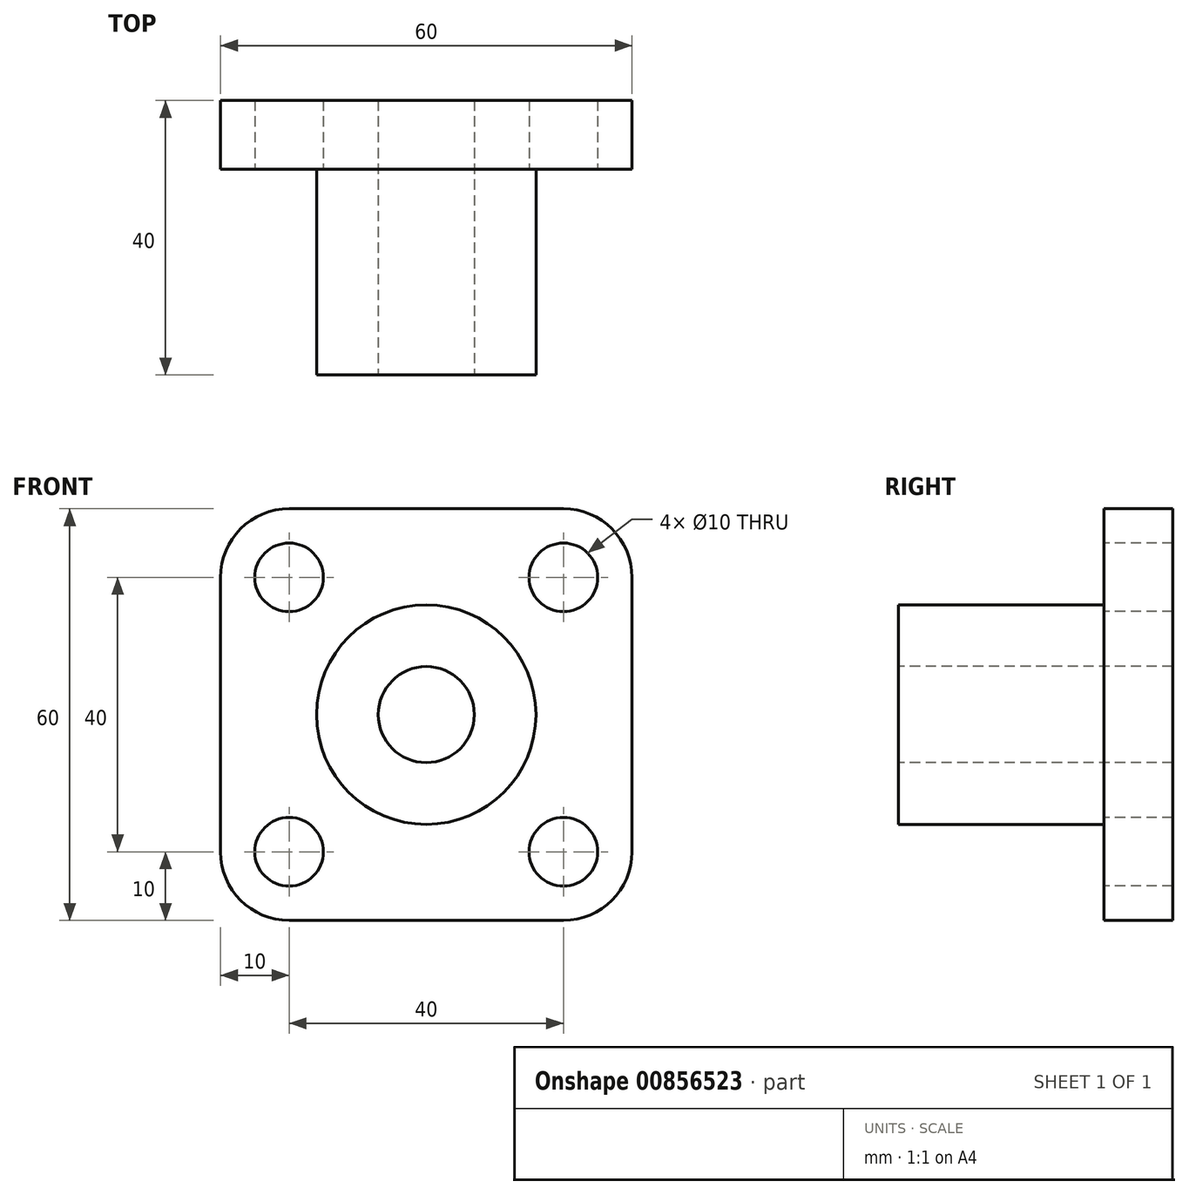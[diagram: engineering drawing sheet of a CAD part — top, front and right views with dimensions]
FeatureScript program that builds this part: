
annotation { "Feature Type Name" : "Feature", "Feature Type Description" : "" }
export const myFeature = defineFeature(function(context is Context, id is Id, definition is map)
    precondition{}
    {
        {
            var Q0;
            Q0=qCreatedBy(makeId("Front.planeOp"),FACE);
            var sketch = newSketch(context, id + "F0", { "sketchPlane" : qUnion([Q0])});
            skLineSegment(sketch, "E0.bottom", {"start": v(30, 30) * mm, "end": v(-30, 30) * mm});
            skLineSegment(sketch, "E0.top", {"start": v(30, -30) * mm, "end": v(-30, -30) * mm});
            skLineSegment(sketch, "E0.left", {"start": v(30, 30) * mm, "end": v(30, -30) * mm});
            skLineSegment(sketch, "E0.right", {"start": v(-30, 30) * mm, "end": v(-30, -30) * mm});
            skPoint(sketch, "E0.middle", {"position": v(0, 0) * mm});
            skSolve(sketch);
        }
        {
            var Q0;
            Q0 = qSketchRegion(id + "F0", true);
            var Q1;
            Q1=makeQuery(id+"F0.imprint","IMPRINT",FACE,{"disambiguationData":[TD([[makeQuery(id+"F0.imprint","IMPRINT",EDGE,{"derivedFrom":sQuery(id+"F0.wireOp",EDGE,"E0.bottom")}),1.0]])]});
            extrude(context, id + "F1", {"entities" : qUnion([Q0, Q1]), "depth" : 10 * mm, "offsetDistance" : 25 * mm});
        }
        {
            var Q0;
            Q0=makeQuery(id+"F1.opExtrude","SWEPT_EDGE",EDGE,{"disambiguationData":[OSD([sQuery(id+"F0.wireOp",EDGE,"E0.bottom"),sQuery(id+"F0.wireOp",EDGE,"E0.left")])]});
            var Q1;
            Q1=makeQuery(id+"F1.opExtrude","SWEPT_EDGE",EDGE,{"disambiguationData":[OSD([sQuery(id+"F0.wireOp",EDGE,"E0.bottom"),sQuery(id+"F0.wireOp",EDGE,"E0.right")])]});
            var Q2;
            Q2=makeQuery(id+"F1.opExtrude","SWEPT_EDGE",EDGE,{"disambiguationData":[OSD([sQuery(id+"F0.wireOp",EDGE,"E0.top"),sQuery(id+"F0.wireOp",EDGE,"E0.left")])]});
            var Q3;
            Q3=makeQuery(id+"F1.opExtrude","SWEPT_EDGE",EDGE,{"disambiguationData":[OSD([sQuery(id+"F0.wireOp",EDGE,"E0.top"),sQuery(id+"F0.wireOp",EDGE,"E0.right")])]});
            fillet(context, id + "F2", {"entities" : qUnion([Q0, Q1, Q2, Q3]), "radius" : 10 * mm, "tangentPropagation" : true, "allowEdgeOverflow" : false});
        }
        {
            var Q0;
            Q0=makeQuery(id+"F1.opExtrude","CAP_FACE",FACE,{"disambiguationData":[OSD([sQuery(id+"F0.wireOp",EDGE,"E0.bottom"),sQuery(id+"F0.wireOp",EDGE,"E0.top"),sQuery(id+"F0.wireOp",EDGE,"E0.left"),sQuery(id+"F0.wireOp",EDGE,"E0.right")])],"isStart":false});
            var sketch = newSketch(context, id + "F3", { "sketchPlane" : qUnion([Q0])});
            skCircle(sketch, "E1", {"center": v(0, 0) * mm, "radius": 16 * mm});
            skSolve(sketch);
        }
        {
            var Q0;
            Q0=makeQuery(id+"F3.imprint","IMPRINT",FACE,{"disambiguationData":[TD([[makeQuery(id+"F3.imprint","IMPRINT",EDGE,{"derivedFrom":sQuery(id+"F3.wireOp",EDGE,"E1")}),1.0]])]});
            extrude(context, id + "F4", {"entities" : qUnion([Q0]), "operationType" : NewBodyOperationType.ADD, "depth" : 30 * mm, "offsetDistance" : 25 * mm});
        }
        {
            var Q0;
            Q0=makeQuery(id+"F4.opExtrude","CAP_FACE",FACE,{"disambiguationData":[OSD([sQuery(id+"F3.wireOp",EDGE,"E1")])],"isStart":false});
            var sketch = newSketch(context, id + "F5", { "sketchPlane" : qUnion([Q0])});
            skPoint(sketch, "E2", {"position": v(0, 0) * mm});
            skSolve(sketch);
        }
        {
            var Q0;
            Q0=sQuery(id+"F5.wireOp",VERTEX,"E2");
            var Q1;
            Q1=makeQuery(id+"F1.opExtrude","SWEPT_BODY",BODY,{"disambiguationData":[OSD([sQuery(id+"F0.wireOp",EDGE,"E0.bottom"),sQuery(id+"F0.wireOp",EDGE,"E0.top"),sQuery(id+"F0.wireOp",EDGE,"E0.left"),sQuery(id+"F0.wireOp",EDGE,"E0.right")])]});
            hole(context, id + "F6", {"style" : HoleStyle.SIMPLE, "endStyle" : HoleEndStyle.THROUGH, "standardTappedOrClearance" : lookupTablePath({ "standard" : "ISO", "engagement" : "75%", "pitch" : "2 mm", "size" : "M16", "type" : "Tapped" }), "standardBlindInLast" : lookupTablePath({ "standard" : "ISO", "engagement" : "75%", "pitch" : "2 mm", "size" : "M16", "type" : "Tapped" }), "holeDiameter" : 14 * mm, "majorDiameter" : 16 * mm, "showTappedDepth" : true, "isTappedThrough" : true, "tappedDepth" : 19 * mm, "tapClearance" : 3, "locations" : qUnion([Q0]), "scope" : qUnion([Q1])});
        }
        {
            var Q0;
            Q0=makeQuery(id+"F4.opExtrude","CAP_FACE",FACE,{"disambiguationData":[OSD([sQuery(id+"F3.wireOp",EDGE,"E1")])],"isStart":false});
            var sketch = newSketch(context, id + "F7", { "sketchPlane" : qUnion([Q0])});
            skLineSegment(sketch, "E3", {"start": v(-20, 34.9) * mm, "end": v(-20, -42.63) * mm, "construction": true});
            skLineSegment(sketch, "E4", {"start": v(-45.01, -20) * mm, "end": v(56.32, -20) * mm, "construction": true});
            skLineSegment(sketch, "E5", {"start": v(50.82, 20) * mm, "end": v(-59.9, 20) * mm, "construction": true});
            skLineSegment(sketch, "E6", {"start": v(20, 34.43) * mm, "end": v(20, -45.41) * mm, "construction": true});
            skPoint(sketch, "E7", {"position": v(-20, 20) * mm});
            skPoint(sketch, "E8", {"position": v(20, 20) * mm});
            skPoint(sketch, "E9", {"position": v(20, -20) * mm});
            skPoint(sketch, "E10", {"position": v(-20, -20) * mm});
            skSolve(sketch);
        }
        {
            var Q0;
            Q0=sQuery(id+"F7.wireOp",VERTEX,"E7");
            var Q1;
            Q1=sQuery(id+"F7.wireOp",VERTEX,"E8");
            var Q2;
            Q2=sQuery(id+"F7.wireOp",VERTEX,"E9");
            var Q3;
            Q3=sQuery(id+"F7.wireOp",VERTEX,"E10");
            var Q4;
            Q4=makeQuery(id+"F1.opExtrude","SWEPT_BODY",BODY,{"disambiguationData":[OSD([sQuery(id+"F0.wireOp",EDGE,"E0.bottom"),sQuery(id+"F0.wireOp",EDGE,"E0.top"),sQuery(id+"F0.wireOp",EDGE,"E0.left"),sQuery(id+"F0.wireOp",EDGE,"E0.right")])]});
            hole(context, id + "F8", {"style" : HoleStyle.SIMPLE, "endStyle" : HoleEndStyle.THROUGH, "holeDiameter" : 10 * mm, "majorDiameter" : 5 * mm, "isTappedThrough" : true, "tappedDepth" : 19 * mm, "tapClearance" : 3, "locations" : qUnion([Q0, Q1, Q2, Q3]), "scope" : qUnion([Q4])});
        }
    });
